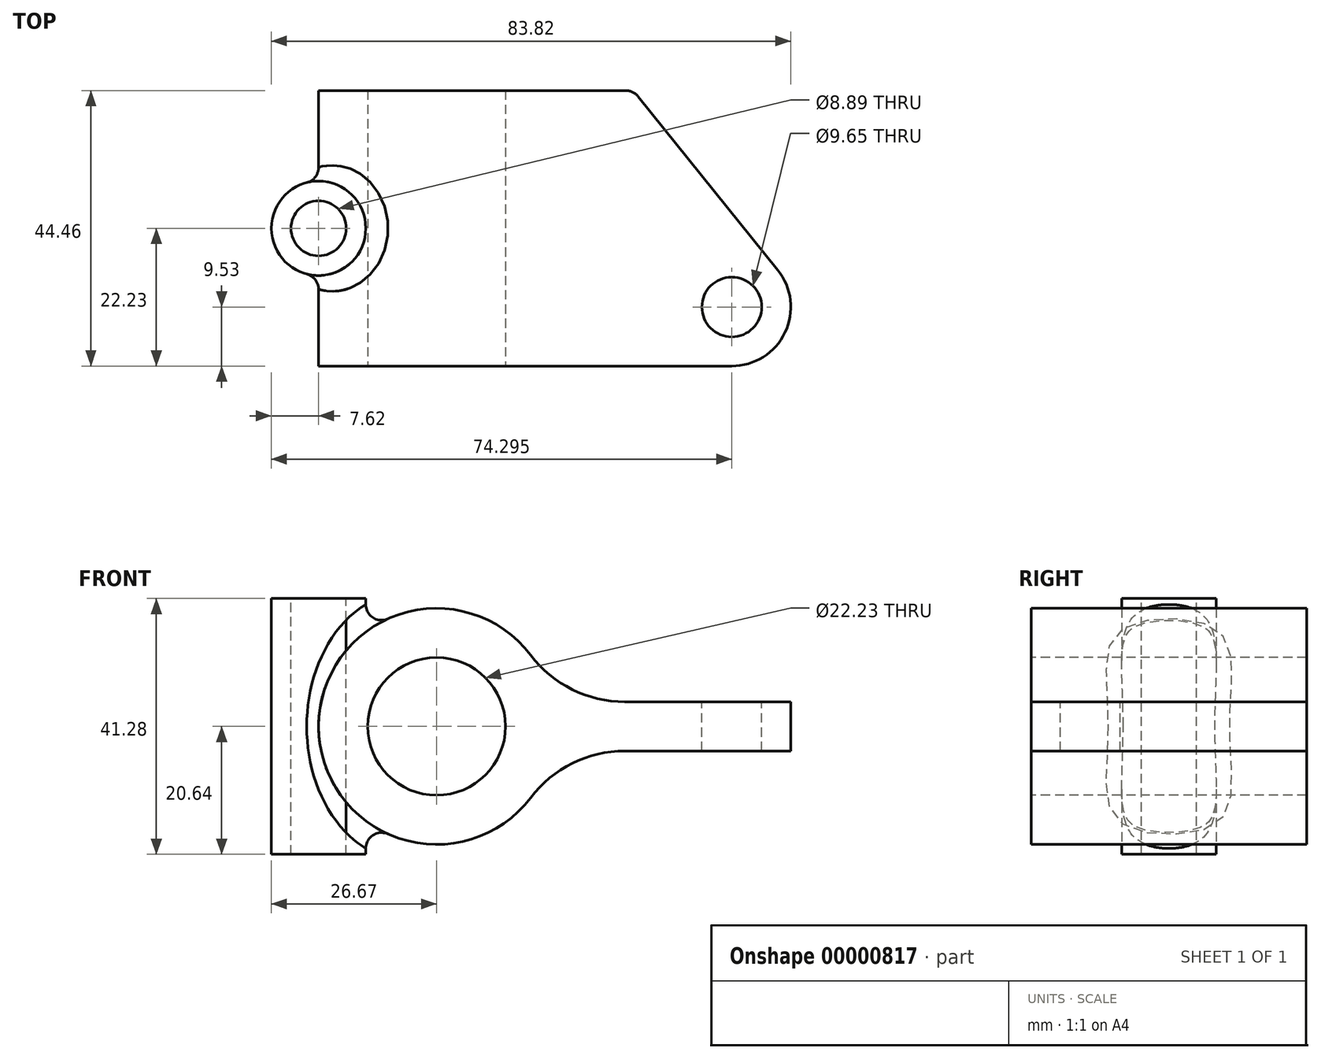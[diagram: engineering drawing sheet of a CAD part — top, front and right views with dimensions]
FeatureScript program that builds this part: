
annotation { "Feature Type Name" : "Feature", "Feature Type Description" : "" }
export const myFeature = defineFeature(function(context is Context, id is Id, definition is map)
    precondition{}
    {
        {
            var Q0;
            Q0=qCreatedBy(makeId("Front.planeOp"),FACE);
            var sketch = newSketch(context, id + "F0", { "sketchPlane" : qUnion([Q0])});
            skCircle(sketch, "E0", {"center": v(0, 0) * mm, "radius": 19.05 * mm});
            skSolve(sketch);
        }
        {
            var Q0;
            Q0=makeQuery(id+"F0.imprint","IMPRINT",FACE,{"disambiguationData":[TD([[makeQuery(id+"F0.imprint","IMPRINT",EDGE,{"derivedFrom":sQuery(id+"F0.wireOp",EDGE,"E0")}),1.0]])]});
            extrude(context, id + "F1", {"entities" : qUnion([Q0]), "endBound" : BoundingType.SYMMETRIC, "depth" : 44.45 * mm});
        }
        {
            var Q0;
            Q0=qCreatedBy(makeId("Top.planeOp"),FACE);
            var sketch = newSketch(context, id + "F2", { "sketchPlane" : qUnion([Q0])});
            skLineSegment(sketch, "E1.0", {"start": v(19.05, -22.23) * mm, "end": v(-19.05, -22.23) * mm});
            skLineSegment(sketch, "E1.1", {"start": v(19.05, 22.23) * mm, "end": v(-19.05, 22.23) * mm});
            skCircle(sketch, "E2", {"center": v(-19.05, 0) * mm, "radius": 7.62 * mm});
            skSolve(sketch);
        }
        {
            var Q0;
            Q0=makeQuery(id+"F2.imprint","IMPRINT",FACE,{"disambiguationData":[TD([[makeQuery(id+"F2.imprint","IMPRINT",EDGE,{"derivedFrom":sQuery(id+"F2.wireOp",EDGE,"E2")}),1.0]])]});
            extrude(context, id + "F3", {"entities" : qUnion([Q0]), "operationType" : NewBodyOperationType.ADD, "endBound" : BoundingType.SYMMETRIC, "depth" : 41.27 * mm});
        }
        {
            var Q0;
            Q0=qCreatedBy(makeId("Top.planeOp"),FACE);
            var sketch = newSketch(context, id + "F4", { "sketchPlane" : qUnion([Q0])});
            skLineSegment(sketch, "E3.0", {"start": v(19.05, 22.23) * mm, "end": v(-19.05, 22.23) * mm});
            skLineSegment(sketch, "E3.1", {"start": v(19.05, -22.23) * mm, "end": v(-19.05, -22.23) * mm});
            skLineSegment(sketch, "E4", {"start": v(0, -22.23) * mm, "end": v(0, 22.23) * mm});
            skLineSegment(sketch, "E5", {"start": v(0, 22.23) * mm, "end": v(31.75, 22.23) * mm});
            skLineSegment(sketch, "E6", {"start": v(31.75, 22.23) * mm, "end": v(55.05, -6.73) * mm});
            skLineSegment(sketch, "E7", {"start": v(19.05, -22.23) * mm, "end": v(47.63, -22.23) * mm});
            skArc(sketch, "E8", {"start": v(47.63, -22.23) * mm, "mid": v(56.22, -16.81) * mm, "end": v(55.05, -6.73) * mm});
            skSolve(sketch);
        }
        {
            var Q0;
            {var subQ3=sQuery(id+"F4.wireOp",EDGE,"E4");Q0=makeQuery(id+"F4.imprint","IMPRINT",FACE,{"disambiguationData":[TD([[makeQuery(id+"F4.imprint","IMPRINT",EDGE,{"derivedFrom":subQ3}),-1.0]])]});}
            extrude(context, id + "F5", {"entities" : qUnion([Q0]), "operationType" : NewBodyOperationType.ADD, "endBound" : BoundingType.SYMMETRIC, "depth" : 7.94 * mm});
        }
        {
            var Q0;
            Q0=makeQuery(id+"F3.opExtrude","CAP_FACE",FACE,{"disambiguationData":[OSD([sQuery(id+"F2.wireOp",EDGE,"E2")])],"isStart":false});
            var sketch = newSketch(context, id + "F6", { "sketchPlane" : qUnion([Q0])});
            skCircle(sketch, "E9.0", {"center": v(-19.05, 0) * mm, "radius": 4.44 * mm});
            skSolve(sketch);
        }
        {
            var Q0;
            Q0=makeQuery(id+"F6.imprint","IMPRINT",FACE,{"disambiguationData":[TD([[makeQuery(id+"F6.imprint","IMPRINT",EDGE,{"derivedFrom":sQuery(id+"F6.wireOp",EDGE,"E9.0")}),1.0]])]});
            extrude(context, id + "F7", {"entities" : qUnion([Q0]), "operationType" : NewBodyOperationType.REMOVE, "endBound" : BoundingType.THROUGH_ALL, "oppositeDirection" : true, "depth" : 25.4 * mm});
        }
        {
            var Q0;
            Q0=makeQuery(id+"F5.boolean.opBoolean","MERGE",FACE,{"derivedFrom":[makeQuery(id+"F1.opExtrude","CAP_FACE",FACE,{"disambiguationData":[OSD([sQuery(id+"F0.wireOp",EDGE,"E0")])],"isStart":false}),makeQuery(id+"F5.opExtrude","SWEPT_FACE",FACE,{"disambiguationData":[OSD([sQuery(id+"F4.wireOp",EDGE,"E3.1")])]})]});
            var sketch = newSketch(context, id + "F8", { "sketchPlane" : qUnion([Q0])});
            skCircle(sketch, "E10", {"center": v(0, 0) * mm, "radius": 11.11 * mm});
            skSolve(sketch);
        }
        {
            var Q0;
            Q0=makeQuery(id+"F8.imprint","IMPRINT",FACE,{"disambiguationData":[TD([[makeQuery(id+"F8.imprint","IMPRINT",EDGE,{"derivedFrom":sQuery(id+"F8.wireOp",EDGE,"E10")}),1.0]])]});
            extrude(context, id + "F9", {"entities" : qUnion([Q0]), "operationType" : NewBodyOperationType.REMOVE, "endBound" : BoundingType.THROUGH_ALL, "oppositeDirection" : true, "depth" : 25.4 * mm});
        }
        {
            var Q0;
            Q0=makeQuery(id+"F5.opExtrude","CAP_FACE",FACE,{"disambiguationData":[OSD([sQuery(id+"F4.wireOp",EDGE,"E3.1"),sQuery(id+"F4.wireOp",EDGE,"E4"),sQuery(id+"F4.wireOp",EDGE,"E5"),sQuery(id+"F4.wireOp",EDGE,"E6"),sQuery(id+"F4.wireOp",EDGE,"E8")])],"isStart":false});
            var sketch = newSketch(context, id + "F10", { "sketchPlane" : qUnion([Q0])});
            skCircle(sketch, "E11", {"center": v(47.63, -12.7) * mm, "radius": 4.83 * mm});
            skSolve(sketch);
        }
        {
            var Q0;
            Q0=makeQuery(id+"F10.imprint","IMPRINT",FACE,{"disambiguationData":[TD([[makeQuery(id+"F10.imprint","IMPRINT",EDGE,{"derivedFrom":sQuery(id+"F10.wireOp",EDGE,"E11")}),1.0]])]});
            extrude(context, id + "F11", {"entities" : qUnion([Q0]), "operationType" : NewBodyOperationType.ADD, "depth" : 25.4 * mm});
        }
        {
            var Q0;
            Q0=makeQuery(id+"F11.opExtrude","CAP_FACE",FACE,{"disambiguationData":[OSD([sQuery(id+"F10.wireOp",EDGE,"E11")])],"isStart":false});
            extrude(context, id + "F12", {"entities" : qUnion([Q0]), "operationType" : NewBodyOperationType.REMOVE, "endBound" : BoundingType.THROUGH_ALL, "oppositeDirection" : true, "depth" : 25.4 * mm});
        }
        {
            var Q0;
            Q0=makeQuery(id+"F5.boolean.opBoolean","INTERSECT",EDGE,{"derivedFrom":[makeQuery(id+"F1.opExtrude","SWEPT_FACE",FACE,{"disambiguationData":[OSD([sQuery(id+"F0.wireOp",EDGE,"E0")])]}),makeQuery(id+"F5.opExtrude","CAP_FACE",FACE,{"disambiguationData":[OSD([sQuery(id+"F4.wireOp",EDGE,"E3.1"),sQuery(id+"F4.wireOp",EDGE,"E4"),sQuery(id+"F4.wireOp",EDGE,"E5"),sQuery(id+"F4.wireOp",EDGE,"E6"),sQuery(id+"F4.wireOp",EDGE,"E8")])],"isStart":false})]});
            var Q1;
            Q1=makeQuery(id+"F5.boolean.opBoolean","INTERSECT",EDGE,{"derivedFrom":[makeQuery(id+"F1.opExtrude","SWEPT_FACE",FACE,{"disambiguationData":[OSD([sQuery(id+"F0.wireOp",EDGE,"E0")])]}),makeQuery(id+"F5.opExtrude","CAP_FACE",FACE,{"disambiguationData":[OSD([sQuery(id+"F4.wireOp",EDGE,"E3.1"),sQuery(id+"F4.wireOp",EDGE,"E4"),sQuery(id+"F4.wireOp",EDGE,"E5"),sQuery(id+"F4.wireOp",EDGE,"E6"),sQuery(id+"F4.wireOp",EDGE,"E8")])],"isStart":true})]});
            fillet(context, id + "F13", {"entities" : qUnion([Q0, Q1]), "radius" : 19.05 * mm, "tangentPropagation" : true, "allowEdgeOverflow" : false});
        }
        {
            var Q0;
            Q0=makeQuery(id+"F5.opExtrude","SWEPT_EDGE",EDGE,{"disambiguationData":[OSD([sQuery(id+"F4.wireOp",EDGE,"E5"),sQuery(id+"F4.wireOp",EDGE,"E6")])]});
            var Q1;
            Q1=makeQuery(id+"F3.boolean.opBoolean","INTERSECT",EDGE,{"derivedFrom":[makeQuery(id+"F1.opExtrude","SWEPT_FACE",FACE,{"disambiguationData":[OSD([sQuery(id+"F0.wireOp",EDGE,"E0")])]}),makeQuery(id+"F3.opExtrude","SWEPT_FACE",FACE,{"disambiguationData":[OSD([sQuery(id+"F2.wireOp",EDGE,"E2")])]})]});
            fillet(context, id + "F14", {"entities" : qUnion([Q0, Q1]), "radius" : 2.54 * mm, "tangentPropagation" : true, "allowEdgeOverflow" : false});
        }
    });
